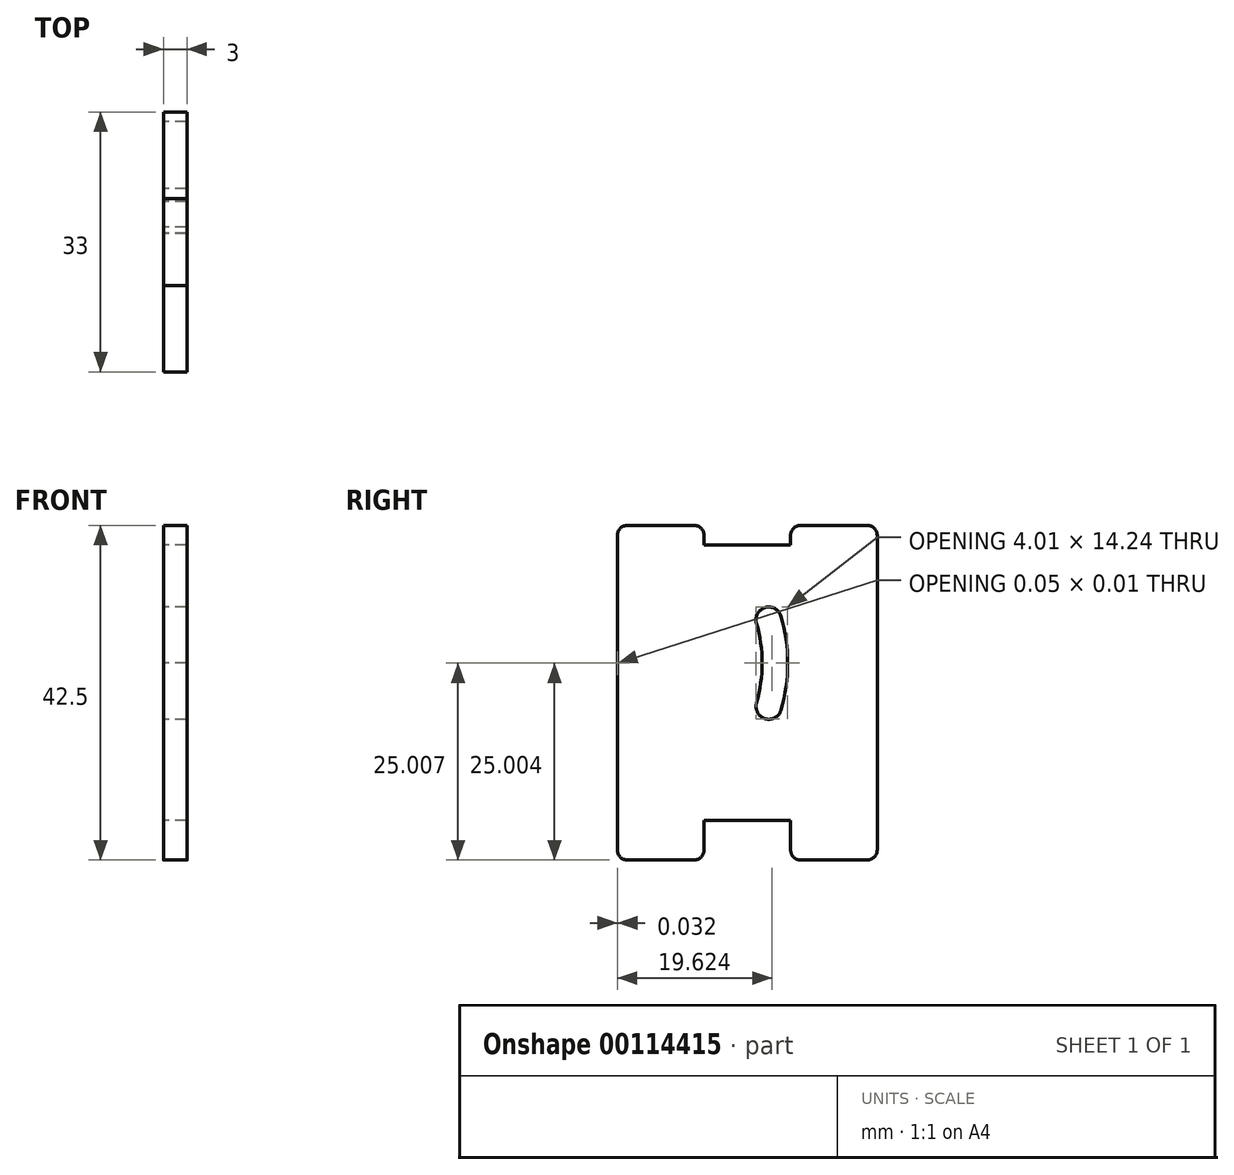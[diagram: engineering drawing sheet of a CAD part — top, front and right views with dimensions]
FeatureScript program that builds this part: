
annotation { "Feature Type Name" : "Feature", "Feature Type Description" : "" }
export const myFeature = defineFeature(function(context is Context, id is Id, definition is map)
    precondition{}
    {
        {
            var Q0;
            Q0=qCreatedBy(makeId("Right.planeOp"),FACE);
            var sketch = newSketch(context, id + "F0", { "sketchPlane" : qUnion([Q0])});
            skPoint(sketch, "E0.middle", {"position": v(0, 0) * mm});
            skLineSegment(sketch, "E1", {"start": v(-16.5, 2.5) * mm, "end": v(1.88, 2.82) * mm});
            skLineSegment(sketch, "E2", {"start": v(-16.49, 2.51) * mm, "end": v(1.17, -2.55) * mm});
            skLineSegment(sketch, "E3", {"start": v(-16.5, 2.5) * mm, "end": v(1.17, 7.56) * mm});
            skArc(sketch, "E4", {"start": v(4.3, 8.46) * mm, "mid": v(2.28, 9.57) * mm, "end": v(1.17, 7.56) * mm});
            skArc(sketch, "E5", {"start": v(1.17, -2.55) * mm, "mid": v(2.29, -4.56) * mm, "end": v(4.3, -3.45) * mm});
            skPoint(sketch, "E6", {"position": v(1.88, 2.82) * mm});
            skPoint(sketch, "E7", {"position": v(1.17, 7.56) * mm});
            skPoint(sketch, "E8", {"position": v(1.17, -2.55) * mm});
            skArc(sketch, "E9", {"start": v(4.3, -3.45) * mm, "mid": v(5.13, 2.5) * mm, "end": v(4.3, 8.46) * mm});
            skArc(sketch, "E10", {"start": v(1.17, -2.55) * mm, "mid": v(1.88, 2.5) * mm, "end": v(1.17, 7.56) * mm});
            skPoint(sketch, "E11.end.orphan", {"position": v(5.13, 2.82) * mm});
            skLineSegment(sketch, "E12.bottom", {"start": v(-5.5, 17.5) * mm, "end": v(5.5, 17.5) * mm});
            skLineSegment(sketch, "E12.top", {"start": v(-15.25, 20) * mm, "end": v(-6.75, 20) * mm});
            skLineSegment(sketch, "E12.left", {"start": v(-16.5, 17.5) * mm, "end": v(-16.5, 18.75) * mm});
            skLineSegment(sketch, "E12.right", {"start": v(16.5, 17.5) * mm, "end": v(16.5, 18.75) * mm});
            skLineSegment(sketch, "E13.bottom", {"start": v(-5.5, -17.5) * mm, "end": v(5.5, -17.5) * mm});
            skLineSegment(sketch, "E13.top", {"start": v(-15.25, -22.5) * mm, "end": v(-6.75, -22.5) * mm});
            skLineSegment(sketch, "E13.left", {"start": v(-16.5, -17.5) * mm, "end": v(-16.5, -21.25) * mm});
            skLineSegment(sketch, "E13.right", {"start": v(16.5, -17.5) * mm, "end": v(16.5, -21.25) * mm});
            skLineSegment(sketch, "E14", {"start": v(5.5, 18.75) * mm, "end": v(5.5, 17.5) * mm});
            skLineSegment(sketch, "E15", {"start": v(-5.5, 18.75) * mm, "end": v(-5.5, 17.5) * mm});
            skLineSegment(sketch, "E16", {"start": v(5.5, -17.5) * mm, "end": v(5.5, -21.25) * mm});
            skLineSegment(sketch, "E17", {"start": v(-5.5, -17.5) * mm, "end": v(-5.5, -21.25) * mm});
            skLineSegment(sketch, "E18.trimOffspring", {"start": v(6.75, 20) * mm, "end": v(15.25, 20) * mm});
            skLineSegment(sketch, "E19.trimOffspring", {"start": v(6.81, -22.5) * mm, "end": v(15.31, -22.5) * mm});
            skPoint(sketch, "E20", {"position": v(-16.5, 18.75) * mm});
            skPoint(sketch, "E21", {"position": v(-5.5, 18.75) * mm});
            skPoint(sketch, "E22", {"position": v(5.5, 18.75) * mm});
            skPoint(sketch, "E23", {"position": v(16.5, 18.75) * mm});
            skPoint(sketch, "E24", {"position": v(16.5, -21.25) * mm});
            skPoint(sketch, "E25", {"position": v(5.5, -21.25) * mm});
            skPoint(sketch, "E26", {"position": v(-5.5, -21.25) * mm});
            skPoint(sketch, "E27", {"position": v(-16.5, -21.25) * mm});
            skPoint(sketch, "E28", {"position": v(15.31, -22.5) * mm});
            skPoint(sketch, "E29", {"position": v(6.81, -22.5) * mm});
            skPoint(sketch, "E30", {"position": v(-6.75, -22.5) * mm});
            skPoint(sketch, "E31", {"position": v(-15.25, -22.5) * mm});
            skPoint(sketch, "E32", {"position": v(-15.25, 20) * mm});
            skPoint(sketch, "E33", {"position": v(-6.75, 20) * mm});
            skPoint(sketch, "E34", {"position": v(6.75, 20) * mm});
            skPoint(sketch, "E35", {"position": v(15.25, 20) * mm});
            skArc(sketch, "E36", {"start": v(-15.25, 20) * mm, "mid": v(-16.13, 19.63) * mm, "end": v(-16.5, 18.75) * mm});
            skArc(sketch, "E37", {"start": v(-5.5, 18.75) * mm, "mid": v(-5.87, 19.63) * mm, "end": v(-6.75, 20) * mm});
            skArc(sketch, "E38", {"start": v(6.75, 20) * mm, "mid": v(5.87, 19.63) * mm, "end": v(5.5, 18.75) * mm});
            skArc(sketch, "E39", {"start": v(16.5, 18.75) * mm, "mid": v(16.13, 19.63) * mm, "end": v(15.25, 20) * mm});
            skArc(sketch, "E40", {"start": v(15.31, -22.5) * mm, "mid": v(16.16, -22.11) * mm, "end": v(16.5, -21.25) * mm});
            skArc(sketch, "E41", {"start": v(5.5, -21.25) * mm, "mid": v(5.89, -22.16) * mm, "end": v(6.81, -22.5) * mm});
            skArc(sketch, "E42", {"start": v(-6.75, -22.5) * mm, "mid": v(-5.87, -22.13) * mm, "end": v(-5.5, -21.25) * mm});
            skArc(sketch, "E43", {"start": v(-16.5, -21.25) * mm, "mid": v(-16.13, -22.13) * mm, "end": v(-15.25, -22.5) * mm});
            skLineSegment(sketch, "E44", {"start": v(16.5, 17.5) * mm, "end": v(5.5, 17.5) * mm});
            skLineSegment(sketch, "E45", {"start": v(-5.5, 17.5) * mm, "end": v(-16.5, 17.5) * mm});
            skLineSegment(sketch, "E46", {"start": v(16.5, -17.5) * mm, "end": v(5.5, -17.5) * mm});
            skLineSegment(sketch, "E47", {"start": v(-5.5, -17.5) * mm, "end": v(-16.5, -17.5) * mm});
            skLineSegment(sketch, "E48", {"start": v(1.88, 2.82) * mm, "end": v(5.13, 2.82) * mm});
            skPoint(sketch, "E49", {"position": v(3.5, 2.82) * mm});
            skLineSegment(sketch, "E50", {"start": v(1.17, 7.56) * mm, "end": v(4.3, 8.46) * mm});
            skLineSegment(sketch, "E51", {"start": v(1.17, -2.55) * mm, "end": v(4.3, -3.45) * mm});
            skLineSegment(sketch, "E52", {"start": v(-16.5, 17.5) * mm, "end": v(-16.5, -17.5) * mm});
            skLineSegment(sketch, "E53", {"start": v(16.5, 17.5) * mm, "end": v(16.5, -17.5) * mm});
            skSolve(sketch);
        }
        {
            var Q0;
            {var subQ2=sQuery(id+"F0.wireOp",EDGE,"E4");Q0=makeQuery(id+"F0.imprint","IMPRINT",FACE,{"disambiguationData":[TD([[makeQuery(id+"F0.imprint","IMPRINT",EDGE,{"derivedFrom":subQ2}),-1.0]])]});}
            var Q1;
            Q1=makeQuery(id+"F0.imprint","IMPRINT",FACE,{"disambiguationData":[TD([[makeQuery(id+"F0.imprint","IMPRINT",EDGE,{"derivedFrom":sQuery(id+"F0.wireOp",EDGE,"E13.top")}),1.0]])]});
            var Q2;
            Q2=makeQuery(id+"F0.imprint","IMPRINT",FACE,{"disambiguationData":[TD([[makeQuery(id+"F0.imprint","IMPRINT",EDGE,{"derivedFrom":sQuery(id+"F0.wireOp",EDGE,"E13.right")}),-1.0]])]});
            var Q3;
            Q3=makeQuery(id+"F0.imprint","IMPRINT",FACE,{"disambiguationData":[TD([[makeQuery(id+"F0.imprint","IMPRINT",EDGE,{"derivedFrom":sQuery(id+"F0.wireOp",EDGE,"E12.right")}),1.0]])]});
            var Q4;
            Q4=makeQuery(id+"F0.imprint","IMPRINT",FACE,{"disambiguationData":[TD([[makeQuery(id+"F0.imprint","IMPRINT",EDGE,{"derivedFrom":sQuery(id+"F0.wireOp",EDGE,"E12.top")}),-1.0]])]});
            var Q5;
            {var subQ3=sQuery(id+"F0.wireOp",EDGE,"E2");var subQ5=sQuery(id+"F0.wireOp",EDGE,"E3");var subQ6=makeQuery(id+"F0.imprint","INTERSECT",VERTEX,{"derivedFrom":[subQ3,subQ5]});Q5=makeQuery(id+"F0.imprint","IMPRINT",FACE,{"disambiguationData":[TD([[makeQuery(id+"F0.imprint","IMPRINT",EDGE,{"disambiguationData":[TD([[subQ6,-1.0]])],"derivedFrom":subQ3}),1.0]])]});}
            var Q6;
            {var subQ1=sQuery(id+"F0.wireOp",EDGE,"E1");var subQ3=sQuery(id+"F0.wireOp",EDGE,"E2");var subQ4=makeQuery(id+"F0.imprint","INTERSECT",VERTEX,{"derivedFrom":[subQ1,subQ3]});Q6=makeQuery(id+"F0.imprint","IMPRINT",FACE,{"disambiguationData":[TD([[makeQuery(id+"F0.imprint","IMPRINT",EDGE,{"disambiguationData":[TD([[subQ4,-1.0]])],"derivedFrom":subQ1}),-1.0]])]});}
            extrude(context, id + "F1", {"entities" : qUnion([Q0, Q1, Q2, Q3, Q4, Q5, Q6]), "depth" : 3 * mm});
        }
    });
